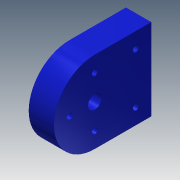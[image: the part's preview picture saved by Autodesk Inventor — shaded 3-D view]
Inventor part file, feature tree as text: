
AUTODESK INVENTOR PART (.ipt)
format: ipt  version: 2013 (Build 170138000, 138)  size: 125,952 bytes
history: native  units: mm
features: sketch x5, extrude x3
ambient origin geometry x8: Origin, YZ Plane, XZ Plane, XY Plane, X Axis, Y Axis, Z Axis, Center Point
bodies: Solid1 (feature_tree)
feature tree (8):
  extrude  "Extrusion1"  Depth=4.0mm TaperAngle=0.0deg
  extrude  "Extrusion2"  [1 undecoded]
  extrude  "Extrusion3"  [1 undecoded]
  sketch  "Sketch4"
  sketch  "Sketch5"
  sketch  "Sketch1"  dims[d0=17.0mm d1=0.0mm d2=4.0mm d3=0.0mm]
  sketch  "Sketch2"  dims[d4=7.0mm d5=0.0mm]
  sketch  "Sketch3"
note: 2 required parameter values undecoded (feature->parameter linkage not recoverable at this tier; creation-order binding heuristic only, values carry confidence <= 0.55)
